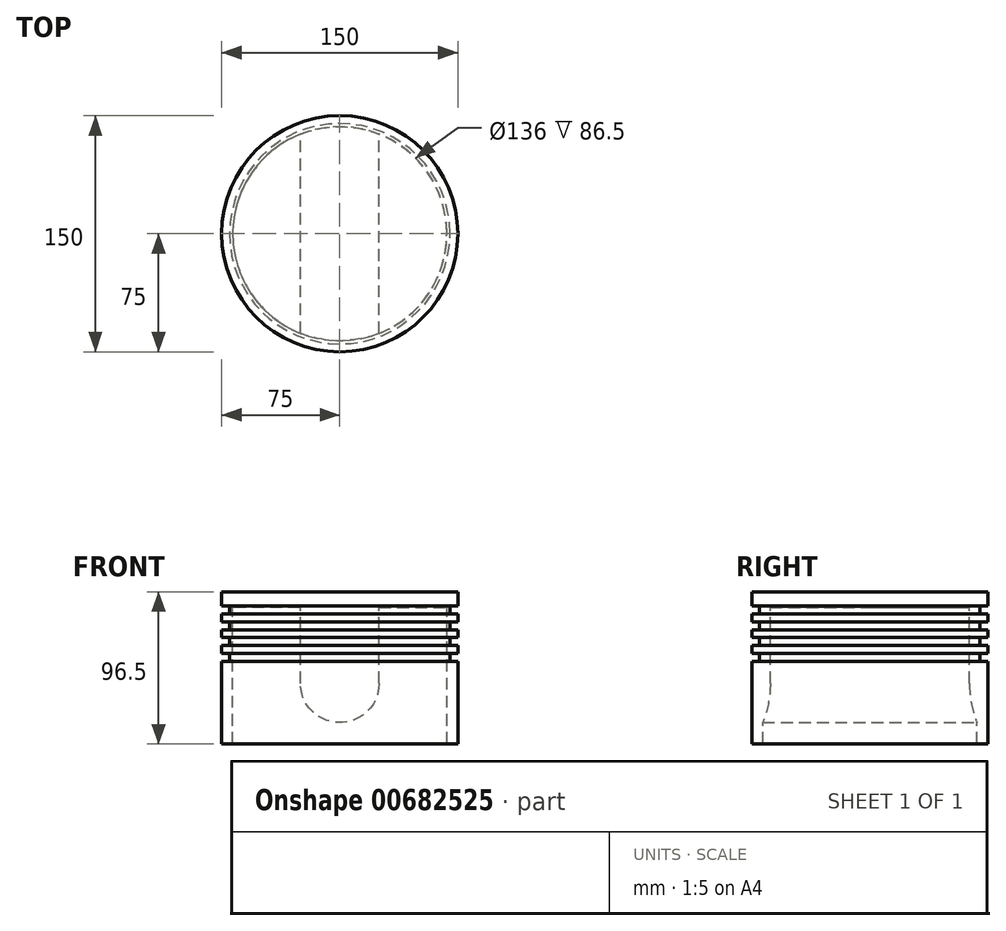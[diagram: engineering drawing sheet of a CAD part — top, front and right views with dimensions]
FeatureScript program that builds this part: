
annotation { "Feature Type Name" : "Feature", "Feature Type Description" : "" }
export const myFeature = defineFeature(function(context is Context, id is Id, definition is map)
    precondition{}
    {
        {
            var Q0;
            Q0=qCreatedBy(makeId("Front.planeOp"),FACE);
            var sketch = newSketch(context, id + "F0", { "sketchPlane" : qUnion([Q0])});
            skLineSegment(sketch, "E0", {"start": v(-75, 50) * mm, "end": v(0, 50) * mm});
            skLineSegment(sketch, "E1", {"start": v(-75, 50) * mm, "end": v(-75, 41) * mm});
            skLineSegment(sketch, "E2", {"start": v(-75, 41) * mm, "end": v(-70, 41) * mm});
            skLineSegment(sketch, "E3", {"start": v(-70, 41) * mm, "end": v(-70, 36) * mm});
            skLineSegment(sketch, "E4", {"start": v(-70, 36) * mm, "end": v(-75, 36) * mm});
            skLineSegment(sketch, "E5", {"start": v(-75, 36) * mm, "end": v(-75, 31) * mm});
            skLineSegment(sketch, "E6", {"start": v(-75, 31) * mm, "end": v(-70, 31) * mm});
            skLineSegment(sketch, "E7", {"start": v(-70, 31) * mm, "end": v(-70, 26) * mm});
            skLineSegment(sketch, "E8", {"start": v(-70, 26) * mm, "end": v(-75, 26) * mm});
            skLineSegment(sketch, "E9", {"start": v(-75, 26) * mm, "end": v(-75, 21) * mm});
            skLineSegment(sketch, "E10", {"start": v(-75, 21) * mm, "end": v(-70, 21) * mm});
            skLineSegment(sketch, "E11", {"start": v(-70, 21) * mm, "end": v(-70, 16) * mm});
            skLineSegment(sketch, "E12", {"start": v(-70, 16) * mm, "end": v(-75, 16) * mm});
            skLineSegment(sketch, "E13", {"start": v(-75, 16) * mm, "end": v(-75, 11) * mm});
            skLineSegment(sketch, "E14", {"start": v(-75, -46.5) * mm, "end": v(-68, -46.5) * mm});
            skLineSegment(sketch, "E15", {"start": v(-68, -46.5) * mm, "end": v(-68, 40) * mm});
            skLineSegment(sketch, "E16", {"start": v(-68, 40) * mm, "end": v(0, 40) * mm});
            skLineSegment(sketch, "E17", {"start": v(0, 85.06) * mm, "end": v(0, -105.28) * mm, "construction": true});
            skLineSegment(sketch, "E18", {"start": v(-75, 11) * mm, "end": v(-70, 11) * mm});
            skLineSegment(sketch, "E19", {"start": v(-70, 11) * mm, "end": v(-70, 6) * mm});
            skLineSegment(sketch, "E20", {"start": v(-70, 6) * mm, "end": v(-75, 6) * mm});
            skLineSegment(sketch, "E21.trimOffspring", {"start": v(-75, 6) * mm, "end": v(-75, -46.5) * mm});
            skPoint(sketch, "E22.orphan", {"position": v(0, -46.5) * mm});
            skLineSegment(sketch, "E23", {"start": v(0, 50) * mm, "end": v(0, 40) * mm});
            skSolve(sketch);
        }
        {
            var Q0;
            Q0 = qSketchRegion(id + "F0", true);
            var Q1;
            Q1=sQuery(id+"F0.wireOp",EDGE,"E17");
            revolve(context, id + "F1", {"entities" : qUnion([Q0]), "axis" : qUnion([Q1]), "revolveType" : RevolveType.FULL});
        }
        {
            var Q0;
            Q0=qCreatedBy(makeId("Front.planeOp"),FACE);
            var sketch = newSketch(context, id + "F2", { "sketchPlane" : qUnion([Q0])});
            skArc(sketch, "E24", {"start": v(-25, -8) * mm, "mid": v(0, -33) * mm, "end": v(25, -8) * mm});
            skLineSegment(sketch, "E25", {"start": v(-25, -8) * mm, "end": v(-25, 40) * mm});
            skLineSegment(sketch, "E26", {"start": v(25, 40) * mm, "end": v(25, -8) * mm});
            skLineSegment(sketch, "E27", {"start": v(-25, 40) * mm, "end": v(25, 40) * mm});
            skSolve(sketch);
        }
        {
            var Q0;
            Q0 = qSketchRegion(id + "F2", true);
            var Q1;
            Q1=makeQuery(id+"F1.opRevolve","SWEPT_FACE",FACE,{"disambiguationData":[OSD([sQuery(id+"F0.wireOp",EDGE,"E15")])]});
            extrude(context, id + "F3", {"entities" : qUnion([Q0]), "operationType" : NewBodyOperationType.ADD, "endBound" : BoundingType.UP_TO_NEXT, "depth" : 25 * mm, "endBoundEntityFace" : qUnion([Q1]), "offsetDistance" : 25.4 * mm, "hasSecondDirection" : true, "secondDirectionBound" : SecondDirectionBoundingType.UP_TO_NEXT, "secondDirectionOppositeDirection" : true, "secondDirectionDepth" : 25 * mm});
        }
    });
